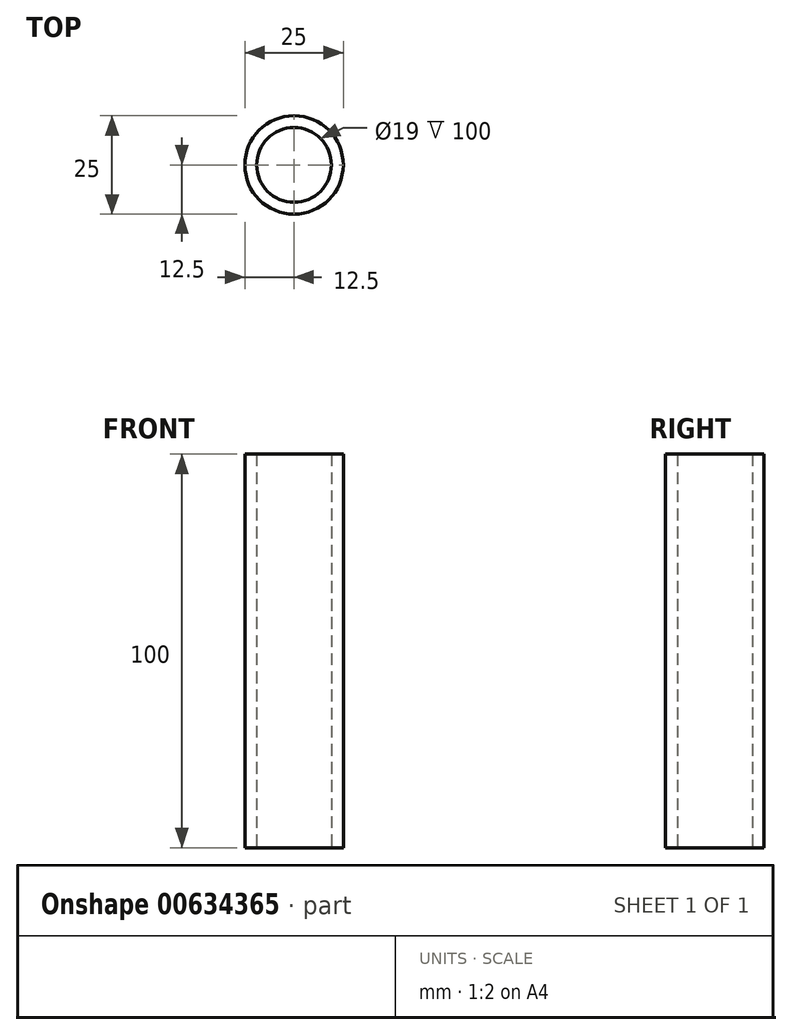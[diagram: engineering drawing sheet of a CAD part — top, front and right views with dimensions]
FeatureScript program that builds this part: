
annotation { "Feature Type Name" : "Feature", "Feature Type Description" : "" }
export const myFeature = defineFeature(function(context is Context, id is Id, definition is map)
    precondition{}
    {
        {
            var Q0;
            Q0=qCreatedBy(makeId("Top.planeOp"),FACE);
            var sketch = newSketch(context, id + "F0", { "sketchPlane" : qUnion([Q0])});
            skCircle(sketch, "E0", {"center": v(0, 0) * mm, "radius": 12.5 * mm});
            skCircle(sketch, "E1", {"center": v(0, 0) * mm, "radius": 9.5 * mm});
            skSolve(sketch);
        }
        {
            var Q0;
            Q0=qSketchRegion(id+"F0",true);
            extrude(context, id + "F1", {"entities" : qUnion([Q0]), "depth" : 100 * mm, "offsetDistance" : 25 * mm});
        }
        {
            var Q0;
            Q0=makeQuery(id+"F1.opExtrude","CAP_FACE",FACE,{"disambiguationData":[OSD([sQuery(id+"F0.wireOp",EDGE,"E0"),sQuery(id+"F0.wireOp",EDGE,"E1")])],"isStart":false});
            var sketch = newSketch(context, id + "F2", { "sketchPlane" : qUnion([Q0])});
            skCircle(sketch, "E2.0", {"center": v(0, 0) * mm, "radius": 9.5 * mm});
            skCircle(sketch, "E3.0", {"center": v(0, 0) * mm, "radius": 12.5 * mm});
            skSolve(sketch);
        }
    });
